# Revit family: 5_天吊埋込タイプ 高静圧 単相100V_3相200V-60
name_source: partatom
category: 機械設備
units: mm (PartAtom-declared; Revit-internal decimal feet)

## family parameters
OmniClass タイトル = Centrifugal Fans
OmniClass 番号 = 23.75.35.17.27
パーツ タイプ = 割り込み
ロード時にボイドで切り取り = いいえ
丸型コネクタ寸法 = 直径を使用
作業面ベース = いいえ
共有 = いいえ
常に垂直 = はい
部屋計算ポイント = はい

## types (13) — shared parameters
Clearance Left = 450  [stored 1.47638 ft]
IfcExportAs = IfcFanType
IfcExportType = CENTRIFUGALFORWARDCURVED
MID静圧 = 0.0 Pa
MID風量 = 0.0 m³/h
OmniClassCode = 23-33 31 19 13 15
URL = https://www.mitsubishielectric.co.jp
Uniclass2015Code = Pr_65_67_29_12
Uniclass2015Title = Centrifugal fans
Uniclass2015Version = Systems v1.9
d1 = 100  [stored 0.328084 ft]
サービススペース = はい
ファンの種類 = 多翼形
仕様書バージョン = Version1.0
企業コード = 108420
分類コード = 50052502100020
周波数 = 60 Hz
呼称 = 消音ボックス付送風機
本体マテリアル = 溶融亜鉛めっき鋼板
極 = 4
法定耐用年数 = 15
盤工事区分 = 電気工事
積算_科目 = 2 換気設備
製品リリース年月 = 2014年6月1日
製品出荷対象 = 国内
製造元 = 三菱電機株式会社
設置方法 = 天吊
説明 = ストレートシロッコファン天吊埋込タイプ（高静圧形）
負荷分類 = 3_ファン類
運転質量 = 0.00 kg
zero-valued in all types: Clearance Back, Clearance Bottom, Clearance Front, Clearance Right, Clearance Top

## per-type parameters (varying)
- BFS-15SKA: Depth=335  [stored 1.09908 ft]; Height=226  [stored 0.74147 ft]; M=60  [stored 0.19685 ft]; MAX静圧=80.0 Pa; MAX風量=150.0 m³/h; MIN静圧=40.0 Pa; MIN風量=105.0 m³/h; Width=223  [stored 0.731627 ft]; ダクト径=100 mm; 価格=36000 $; 天吊金具ピッチ奥行=299  [stored 0.980971 ft]; 天吊金具ピッチ幅=299  [stored 0.980971 ft]; 形名=BFS-SKA : BFS-15SKA; 極数=2; 消費電力=28 W; 番手=#1; 相=1; 製品質量=5.20 kg; 質量=6.24 kg; 電動機出力=8 W; 電圧=100 V; 騒音レベル(dB(A))=38; 騒音レベル(dB(A))_側面=24.5; 騒音レベル(dB(A))_吐出=38; 騒音レベル(dB(A))_吸込=33
- BFS-30SKA: Depth=335  [stored 1.09908 ft]; Height=226  [stored 0.74147 ft]; M=70  [stored 0.229659 ft]; MAX静圧=90.0 Pa; MAX風量=300.0 m³/h; MIN静圧=40.0 Pa; MIN風量=220.0 m³/h; Width=223  [stored 0.731627 ft]; ダクト径=150 mm; 価格=45100 $; 天吊金具ピッチ奥行=299  [stored 0.980971 ft]; 天吊金具ピッチ幅=299  [stored 0.980971 ft]; 形名=BFS-SKA : BFS-30SKA; 極数=2; 消費電力=62 W; 番手=#1; 相=1; 製品質量=5.30 kg; 質量=6.36 kg; 電動機出力=12 W; 電圧=100 V; 騒音レベル(dB(A))=46; 騒音レベル(dB(A))_側面=30; 騒音レベル(dB(A))_吐出=46; 騒音レベル(dB(A))_吸込=43
- BFS-40SKA: Depth=389  [stored 1.27625 ft]; Height=255  [stored 0.836614 ft]; M=70  [stored 0.229659 ft]; MAX静圧=110.0 Pa; MAX風量=400.0 m³/h; MIN静圧=55.0 Pa; MIN風量=280.0 m³/h; Width=255  [stored 0.836614 ft]; ダクト径=150 mm; 価格=53200 $; 天吊金具ピッチ奥行=353  [stored 1.15814 ft]; 天吊金具ピッチ幅=331  [stored 1.08596 ft]; 形名=BFS-SKA : BFS-40SKA; 極数=2; 消費電力=81 W; 番手=#1 1/4; 相=1; 製品質量=7.00 kg; 質量=8.40 kg; 電動機出力=30 W; 電圧=100 V; 騒音レベル(dB(A))=48.5; 騒音レベル(dB(A))_側面=31.5; 騒音レベル(dB(A))_吐出=48.5; 騒音レベル(dB(A))_吸込=43.5
- BFS-50SKA: Depth=431  [stored 1.41404 ft]; Height=255  [stored 0.836614 ft]; M=85  [stored 0.278871 ft]; MAX静圧=200.0 Pa; MAX風量=500.0 m³/h; MIN静圧=125.0 Pa; MIN風量=380.0 m³/h; Width=319  [stored 1.04659 ft]; ダクト径=200 mm; 価格=74300 $; 天吊金具ピッチ奥行=395  [stored 1.29593 ft]; 天吊金具ピッチ幅=395  [stored 1.29593 ft]; 形名=BFS-SKA : BFS-50SKA; 極数=2; 消費電力=102 W; 番手=#1 1/4; 相=1; 製品質量=8.80 kg; 質量=10.56 kg; 電動機出力=45 W; 電圧=100 V; 騒音レベル(dB(A))=51.5; 騒音レベル(dB(A))_側面=32; 騒音レベル(dB(A))_吐出=51.5; 騒音レベル(dB(A))_吸込=44.5
- BFS-65SKA: Depth=489  [stored 1.60433 ft]; Height=305  [stored 1.00066 ft]; M=85  [stored 0.278871 ft]; MAX静圧=220.0 Pa; MAX風量=650.0 m³/h; MIN静圧=100.0 Pa; MIN風量=460.0 m³/h; Width=373  [stored 1.22375 ft]; ダクト径=200 mm; 価格=78800 $; 天吊金具ピッチ奥行=452  [stored 1.48294 ft]; 天吊金具ピッチ幅=449  [stored 1.4731 ft]; 形名=BFS-SKA : BFS-65SKA; 極数=2; 消費電力=156 W; 番手=#1 1/4; 相=1; 製品質量=11.10 kg; 質量=13.32 kg; 電動機出力=75 W; 電圧=100 V; 騒音レベル(dB(A))=53; 騒音レベル(dB(A))_側面=33; 騒音レベル(dB(A))_吐出=53; 騒音レベル(dB(A))_吸込=45.5
- BFS-80SKA: Depth=489  [stored 1.60433 ft]; Height=305  [stored 1.00066 ft]; M=85  [stored 0.278871 ft]; MAX静圧=230.0 Pa; MAX風量=800.0 m³/h; MIN静圧=140.0 Pa; MIN風量=600.0 m³/h; Width=373  [stored 1.22375 ft]; ダクト径=200 mm; 価格=84500 $; 天吊金具ピッチ奥行=452  [stored 1.48294 ft]; 天吊金具ピッチ幅=449  [stored 1.4731 ft]; 形名=BFS-SKA : BFS-80SKA; 極数=2; 消費電力=203 W; 番手=#1 1/4; 相=1; 製品質量=11.10 kg; 質量=13.32 kg; 電動機出力=105 W; 電圧=100 V; 騒音レベル(dB(A))=56; 騒音レベル(dB(A))_側面=36; 騒音レベル(dB(A))_吐出=56; 騒音レベル(dB(A))_吸込=48
- BFS-100SKA: Depth=528  [stored 1.73228 ft]; Height=350  [stored 1.14829 ft]; M=85  [stored 0.278871 ft]; MAX静圧=310.0 Pa; MAX風量=1000.0 m³/h; MIN静圧=200.0 Pa; MIN風量=800.0 m³/h; Width=363  [stored 1.19094 ft]; ダクト径=200 mm; 価格=94000 $; 天吊金具ピッチ奥行=492  [stored 1.61417 ft]; 天吊金具ピッチ幅=440  [stored 1.44357 ft]; 形名=BFS-SKA : BFS-100SKA; 極数=2; 消費電力=356 W; 番手=#1 1/2; 相=1; 製品質量=15.40 kg; 質量=18.48 kg; 電動機出力=180 W; 電圧=100 V; 騒音レベル(dB(A))=61; 騒音レベル(dB(A))_側面=40.5; 騒音レベル(dB(A))_吐出=61; 騒音レベル(dB(A))_吸込=51
- BFS-120SKA: Depth=591  [stored 1.93898 ft]; Height=350  [stored 1.14829 ft]; M=85  [stored 0.278871 ft]; MAX静圧=330.0 Pa; MAX風量=1200.0 m³/h; MIN静圧=175.0 Pa; MIN風量=880.0 m³/h; Width=390  [stored 1.27953 ft]; ダクト径=250 mm; 価格=101300 $; 天吊金具ピッチ奥行=554  [stored 1.81759 ft]; 天吊金具ピッチ幅=467  [stored 1.53215 ft]; 形名=BFS-SKA : BFS-120SKA; 極数=2; 消費電力=388 W; 番手=#1 1/2; 相=1; 製品質量=16.40 kg; 質量=19.68 kg; 電動機出力=200 W; 電圧=100 V; 騒音レベル(dB(A))=61.5; 騒音レベル(dB(A))_側面=41; 騒音レベル(dB(A))_吐出=61.5; 騒音レベル(dB(A))_吸込=51.5
- BFS-150SKA: Depth=591  [stored 1.93898 ft]; Height=350  [stored 1.14829 ft]; M=85  [stored 0.278871 ft]; MAX静圧=350.0 Pa; MAX風量=1500.0 m³/h; MIN静圧=235.0 Pa; MIN風量=1220.0 m³/h; Width=390  [stored 1.27953 ft]; ダクト径=250 mm; 価格=108200 $; 天吊金具ピッチ奥行=554  [stored 1.81759 ft]; 天吊金具ピッチ幅=467  [stored 1.53215 ft]; 形名=BFS-SKA : BFS-150SKA; 極数=2; 消費電力=560 W; 番手=#1 1/2; 相=1; 製品質量=16.60 kg; 質量=19.92 kg; 電動機出力=300 W; 電圧=100 V; 騒音レベル(dB(A))=63.5; 騒音レベル(dB(A))_側面=44; 騒音レベル(dB(A))_吐出=63.5; 騒音レベル(dB(A))_吸込=55
- BFS-80TKA: Depth=489  [stored 1.60433 ft]; Height=305  [stored 1.00066 ft]; M=85  [stored 0.278871 ft]; MAX静圧=260.0 Pa; MAX風量=800.0 m³/h; MIN静圧=145.0 Pa; MIN風量=600.0 m³/h; Width=373  [stored 1.22375 ft]; ダクト径=200 mm; 価格=84500 $; 天吊金具ピッチ奥行=452  [stored 1.48294 ft]; 天吊金具ピッチ幅=449  [stored 1.4731 ft]; 形名=BFS-TKA : BFS-80TKA; 極数=3; 消費電力=190 W; 番手=#1 1/4; 相=3; 製品質量=12.20 kg; 質量=14.64 kg; 電動機出力=170 W; 電圧=200 V; 騒音レベル(dB(A))=57; 騒音レベル(dB(A))_側面=35; 騒音レベル(dB(A))_吐出=57; 騒音レベル(dB(A))_吸込=48
- BFS-100TKA: Depth=528  [stored 1.73228 ft]; Height=350  [stored 1.14829 ft]; M=85  [stored 0.278871 ft]; MAX静圧=320.0 Pa; MAX風量=1000.0 m³/h; MIN静圧=140.0 Pa; MIN風量=670.0 m³/h; Width=363  [stored 1.19094 ft]; ダクト径=200 mm; 価格=94000 $; 天吊金具ピッチ奥行=492  [stored 1.61417 ft]; 天吊金具ピッチ幅=440  [stored 1.44357 ft]; 形名=BFS-TKA : BFS-100TKA; 極数=3; 消費電力=326 W; 番手=#1 1/2; 相=3; 製品質量=14.50 kg; 質量=17.40 kg; 電動機出力=200 W; 電圧=200 V; 騒音レベル(dB(A))=61.5; 騒音レベル(dB(A))_側面=40.5; 騒音レベル(dB(A))_吐出=61.5; 騒音レベル(dB(A))_吸込=50.5
- BFS-120TKA: Depth=591  [stored 1.93898 ft]; Height=350  [stored 1.14829 ft]; M=85  [stored 0.278871 ft]; MAX静圧=370.0 Pa; MAX風量=1200.0 m³/h; MIN静圧=175.0 Pa; MIN風量=830.0 m³/h; Width=390  [stored 1.27953 ft]; ダクト径=250 mm; 価格=101300 $; 天吊金具ピッチ奥行=554  [stored 1.81759 ft]; 天吊金具ピッチ幅=467  [stored 1.53215 ft]; 形名=BFS-TKA : BFS-120TKA; 極数=3; 消費電力=397 W; 番手=#1 1/2; 相=3; 製品質量=16.50 kg; 質量=19.80 kg; 電動機出力=200 W; 電圧=200 V; 騒音レベル(dB(A))=62; 騒音レベル(dB(A))_側面=41; 騒音レベル(dB(A))_吐出=62; 騒音レベル(dB(A))_吸込=51.5
- BFS-150TKA: Depth=591  [stored 1.93898 ft]; Height=350  [stored 1.14829 ft]; M=85  [stored 0.278871 ft]; MAX静圧=370.0 Pa; MAX風量=1500.0 m³/h; MIN静圧=200.0 Pa; MIN風量=1110.0 m³/h; Width=390  [stored 1.27953 ft]; ダクト径=250 mm; 価格=108200 $; 天吊金具ピッチ奥行=554  [stored 1.81759 ft]; 天吊金具ピッチ幅=467  [stored 1.53215 ft]; 形名=BFS-TKA : BFS-150TKA; 極数=3; 消費電力=518 W; 番手=#1 1/2; 相=3; 製品質量=16.50 kg; 質量=19.80 kg; 電動機出力=300 W; 電圧=200 V; 騒音レベル(dB(A))=63.5; 騒音レベル(dB(A))_側面=42.5; 騒音レベル(dB(A))_吐出=63.5; 騒音レベル(dB(A))_吸込=55

note: column(s) folded — value = type name in every type: モデル

note: [stored X ft] marks values corroborated as IEEE doubles in the binary element streams (Revit-internal decimal feet)
